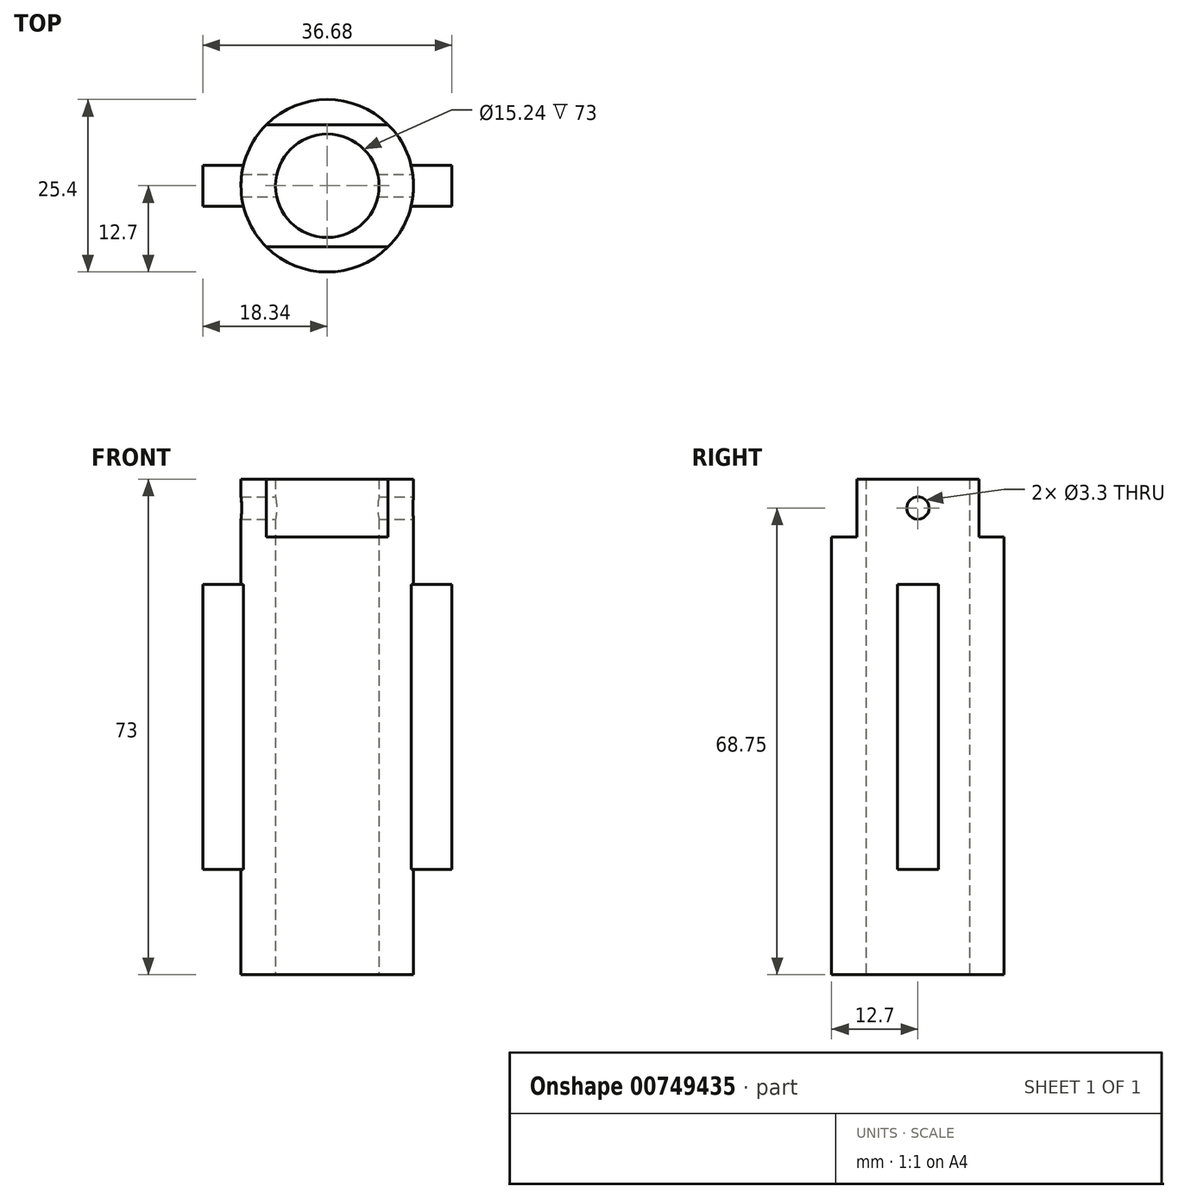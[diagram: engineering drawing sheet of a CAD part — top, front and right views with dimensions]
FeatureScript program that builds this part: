
annotation { "Feature Type Name" : "Feature", "Feature Type Description" : "" }
export const myFeature = defineFeature(function(context is Context, id is Id, definition is map)
    precondition{}
    {
        {
            var Q0;
            Q0=qCreatedBy(makeId("Top.planeOp"),FACE);
            var sketch = newSketch(context, id + "F0", { "sketchPlane" : qUnion([Q0])});
            skCircle(sketch, "E0", {"center": v(0, 0) * mm, "radius": 12.7 * mm});
            skCircle(sketch, "E1", {"center": v(0, 0) * mm, "radius": 7.62 * mm});
            skSolve(sketch);
        }
        {
            var Q0;
            Q0 = qSketchRegion(id + "F0", true);
            extrude(context, id + "F1", {"entities" : qUnion([Q0]), "endBound" : BoundingType.SYMMETRIC, "depth" : 73 * mm, "offsetDistance" : 25 * mm});
        }
        {
            var Q0;
            Q0=qCreatedBy(makeId("Top.planeOp"),FACE);
            var sketch = newSketch(context, id + "F2", { "sketchPlane" : qUnion([Q0])});
            skLineSegment(sketch, "E2.bottom", {"start": v(18.34, -3) * mm, "end": v(12.34, -3) * mm});
            skLineSegment(sketch, "E2.top", {"start": v(18.34, 3) * mm, "end": v(12.34, 3) * mm});
            skLineSegment(sketch, "E2.left", {"start": v(18.34, -3) * mm, "end": v(18.34, 3) * mm});
            skPoint(sketch, "E2.middle", {"position": v(15.7, 0) * mm});
            skArc(sketch, "E3.0", {"start": v(12.34, -3) * mm, "mid": v(12.7, 0) * mm, "end": v(12.34, 3) * mm});
            skPoint(sketch, "E2.right.end.orphan", {"position": v(13.05, 3) * mm});
            skPoint(sketch, "E4.orphan", {"position": v(13.05, -3) * mm});
            skLineSegment(sketch, "E5", {"start": v(0, 5.32) * mm, "end": v(0, -3.69) * mm, "construction": true});
            skLineSegment(sketch, "E6.MirrorCS", {"start": v(-18.34, 3) * mm, "end": v(-12.34, 3) * mm});
            skLineSegment(sketch, "E7.MirrorCS", {"start": v(-18.34, -3) * mm, "end": v(-18.34, 3) * mm});
            skLineSegment(sketch, "E8.MirrorCS", {"start": v(-18.34, -3) * mm, "end": v(-12.34, -3) * mm});
            skArc(sketch, "E9.MirrorCS", {"start": v(-12.34, -3) * mm, "mid": v(-12.7, 0) * mm, "end": v(-12.34, 3) * mm});
            skSolve(sketch);
        }
        {
            var Q0;
            Q0 = qSketchRegion(id + "F2", true);
            extrude(context, id + "F3", {"entities" : qUnion([Q0]), "operationType" : NewBodyOperationType.ADD, "endBound" : BoundingType.SYMMETRIC, "depth" : 42 * mm, "offsetDistance" : 25 * mm});
        }
        {
            var Q0;
            Q0=makeQuery(id+"F1.opExtrude","CAP_FACE",FACE,{"disambiguationData":[OSD([sQuery(id+"F0.wireOp",EDGE,"E0"),sQuery(id+"F0.wireOp",EDGE,"E1")])],"isStart":false});
            var sketch = newSketch(context, id + "F4", { "sketchPlane" : qUnion([Q0])});
            skLineSegment(sketch, "E10.bottom", {"start": v(21.53, -9) * mm, "end": v(-21.53, -9) * mm});
            skLineSegment(sketch, "E10.top", {"start": v(21.53, 9) * mm, "end": v(-21.53, 9) * mm});
            skPoint(sketch, "E10.middle", {"position": v(0, 0) * mm});
            skLineSegment(sketch, "E11", {"start": v(-21.53, 9) * mm, "end": v(-21.53, 15.77) * mm});
            skLineSegment(sketch, "E12", {"start": v(-21.53, 15.77) * mm, "end": v(21.53, 15.77) * mm});
            skLineSegment(sketch, "E13", {"start": v(21.53, 15.77) * mm, "end": v(21.53, 9) * mm});
            skLineSegment(sketch, "E14", {"start": v(21.53, -9) * mm, "end": v(21.53, -17.2) * mm});
            skLineSegment(sketch, "E15", {"start": v(21.53, -17.2) * mm, "end": v(-21.53, -17.2) * mm});
            skLineSegment(sketch, "E16", {"start": v(-21.53, -17.2) * mm, "end": v(-21.53, -9) * mm});
            skSolve(sketch);
        }
        {
            var Q0;
            Q0 = qSketchRegion(id + "F4", true);
            extrude(context, id + "F5", {"entities" : qUnion([Q0]), "operationType" : NewBodyOperationType.REMOVE, "oppositeDirection" : true, "depth" : 8.5 * mm, "offsetDistance" : 25 * mm});
        }
        {
            var Q0;
            Q0=qCreatedBy(makeId("Right.planeOp"),FACE);
            cPlane(context, id + "F6", {"entities" : qUnion([Q0]), "cplaneType" : CPlaneType.OFFSET, "offset" : (25.4 / 2) * mm, "width" : 150 * mm, "height" : 150 * mm});
        }
        {
            var Q0;
            Q0=qCreatedBy(id+"F6.planeOp",FACE);
            var sketch = newSketch(context, id + "F7", { "sketchPlane" : qUnion([Q0])});
            skPoint(sketch, "E17", {"position": v(0, 32.25) * mm});
            skSolve(sketch);
        }
        {
            var Q0;
            Q0=sQuery(id+"F7.wireOp",VERTEX,"E17");
            var Q1;
            Q1=makeQuery(id+"F1.opExtrude","SWEPT_BODY",BODY,{"disambiguationData":[OSD([sQuery(id+"F0.wireOp",EDGE,"E0"),sQuery(id+"F0.wireOp",EDGE,"E1")])]});
            hole(context, id + "F8", {"style" : HoleStyle.SIMPLE, "endStyle" : HoleEndStyle.BLIND, "standardTappedOrClearance" : lookupTablePath({ "standard" : "ISO", "engagement" : "75%", "pitch" : "0.7 mm", "size" : "M4", "type" : "Tapped" }), "standardBlindInLast" : lookupTablePath({ "standard" : "ISO", "engagement" : "75%", "pitch" : "0.7 mm", "size" : "M4", "type" : "Tapped" }), "holeDiameter" : 3.3 * mm, "majorDiameter" : 4 * mm, "showTappedDepth" : true, "holeDepth" : 30 * mm, "isTappedThrough" : true, "tappedDepth" : 27.9 * mm, "tapClearance" : 3, "startFromSketch" : true, "locations" : qUnion([Q0]), "scope" : qUnion([Q1])});
        }
    });
